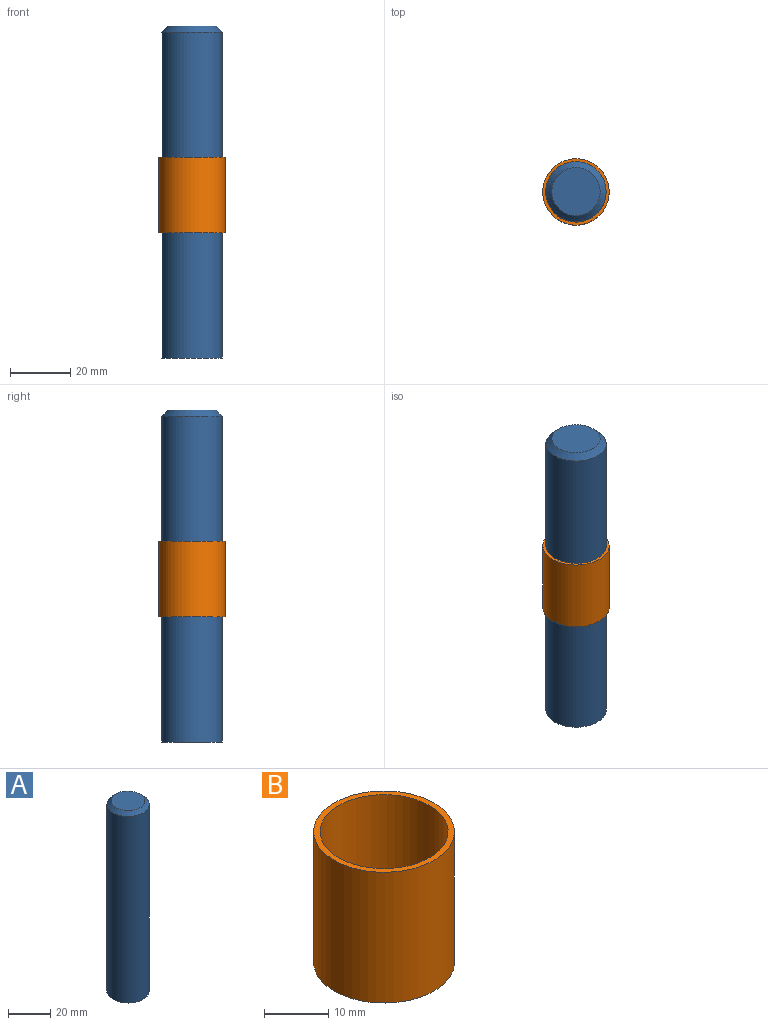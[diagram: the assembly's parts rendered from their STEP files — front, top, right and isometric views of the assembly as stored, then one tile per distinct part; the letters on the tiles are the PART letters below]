
ASSEMBLY  parts=2 mates=1
PART A: 4 faces, bbox 20x20x110 mm
  f0: cylinder r=10mm len=108mm, axis (0,0,-1), area 6785.8mm2, adj f2,f3
  f1: plane 16x16mm, normal (0,0,1), area 201.1mm2, adj f3
  f2: plane 20x20mm, normal (0,0,-1), area 314.2mm2, adj f0
  f3: cone r=8mm half-angle=45deg, axis (0,0,-1), area 159.9mm2, adj f0,f1
PART B: 4 faces, bbox 22x22x25 mm
  f0: cylinder r=10mm len=25mm, axis (0,0,-1), area 1570.8mm2, adj f2,f3
  f1: cylinder r=11mm len=25mm, axis (0,0,-1), area 1727.9mm2, adj f2,f3
  f2: plane 22x22mm, normal (0,0,1), area 66mm2, adj f0,f1
  f3: plane 22x22mm, normal (0,0,-1), area 66mm2, adj f0,f1
PLACE A at identity fixed
PLACE B t=(-89.19,0,41.5)mm
MATE slider B.f0 <-> A.f0  axis (0,0,-1) through (-55.15,0,54)mm
